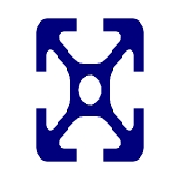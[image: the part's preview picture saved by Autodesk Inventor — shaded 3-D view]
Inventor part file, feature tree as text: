
AUTODESK INVENTOR PART (.ipt)
format: ipt  version: 2020 (Build 240168000, 168)  size: 274,944 bytes
history: native  units: mm
features: other x16, sketch x8
ambient origin geometry x8: Origin, YZ Plane, XZ Plane, XY Plane, X Axis, Y Axis, Z Axis, Center Point
bodies: Body (feature_tree)
feature tree (24):
  other  "Řízená délka"
  other  "Těleso1"
  other  "Start Plane"
  other  "End Plane"
  other  "iFeatureSketch"
  other  "DRAZKA_20:1"
  other  "DRAZKA_20:2"
  other  "DRAZKA_20:3"
  other  "DRAZKA_20:4"
  other  "DIRA_20:1"
  other  "DRAZKA_20:1Axis"
  other  "DRAZKA_20:2Axis"
  other  "DRAZKA_20:3Axis"
  other  "DRAZKA_20:4Axis"
  other  "DIRA_20:1Axis"
  sketch  "Sketch"  dims[d2=20.0mm d3=20.0mm d4=2.0mm d9=-0.0mm d10=110.0mm d11=0.13mm d12=0.0mm d15=0.83mm d16=0.83mm d17=9.8mm d18=3.0mm d19=4.55mm d20=45.0deg d21=5.2mm d22=1.8mm d24=1.0mm d26=0.83mm d27=0.83mm d28=9.8mm d29=3.0mm d30=4.55mm d31=45.0deg d32=5.2mm d33=1.8mm d35=1.0mm d37=0.83mm d38=0.83mm d39=9.8mm d40=3.0mm d41=4.55mm d42=45.0deg d43=5.2mm d44=1.8mm d46=1.0mm d48=0.83mm d49=0.83mm d50=9.8mm d51=3.0mm d52=4.55mm d53=45.0deg d54=5.2mm d55=1.8mm d57=1.0mm d59=4.3mm d60=0.0mm d61=0.0mm d62=0.0mm d63=0.0mm d64=0.0mm d65=0.0mm d66=0.0mm d67=0.0mm d76=90.0deg d14=110.0mm]
  sketch  "Náčrt11"
  other  "Pracovní rovina4"
  sketch  "Náčrt12"
  sketch  "Náčrt6"
  sketch  "Náčrt7"
  sketch  "Náčrt8"
  sketch  "Náčrt9"
  sketch  "Náčrt10"
